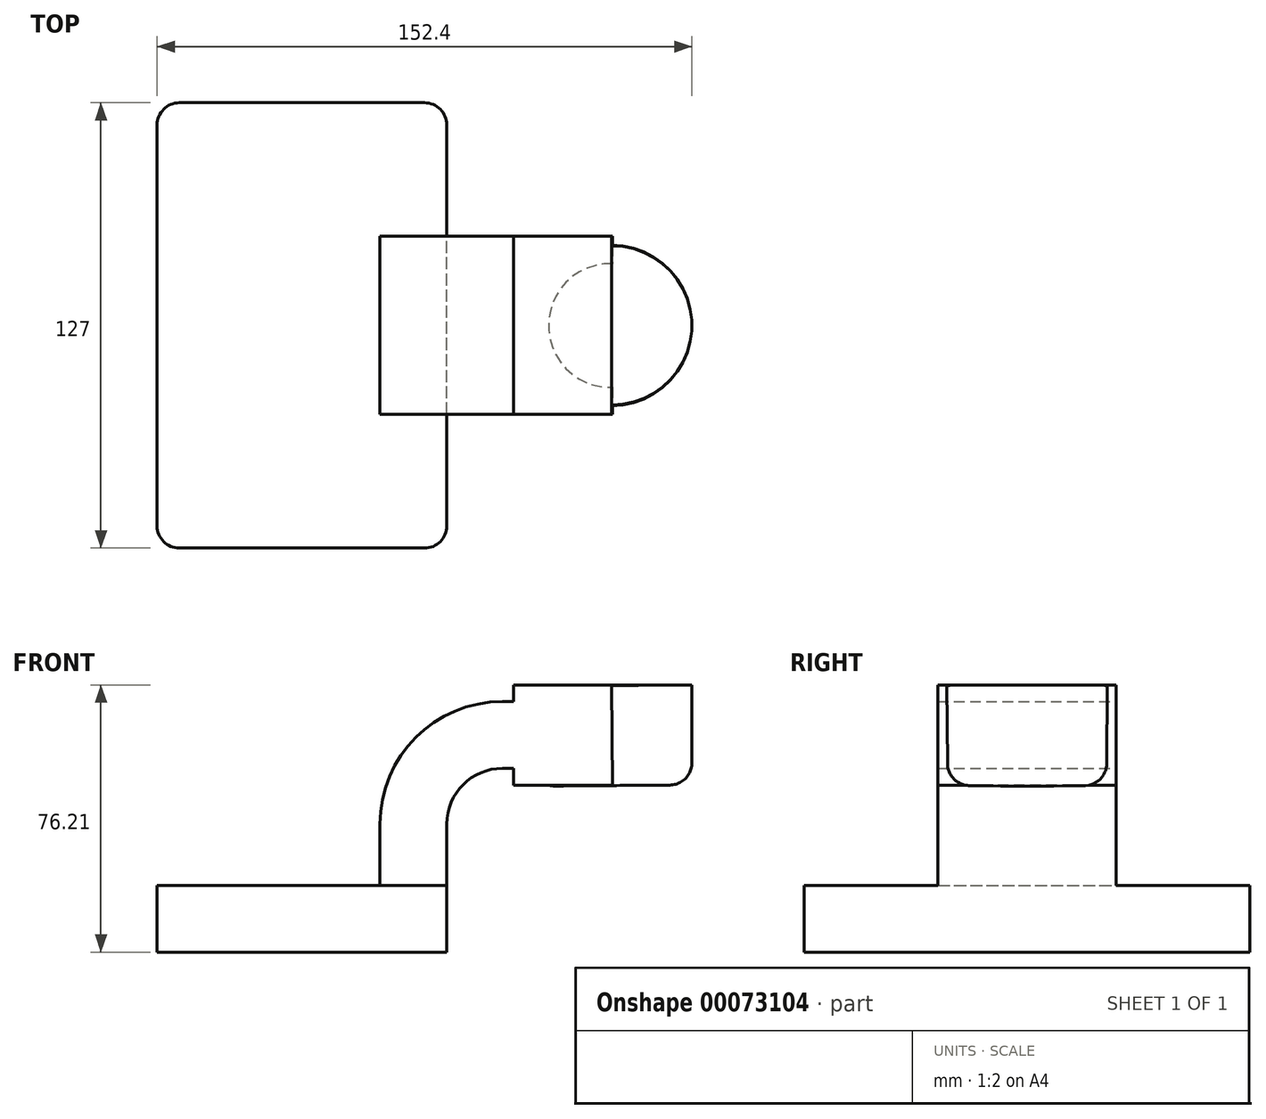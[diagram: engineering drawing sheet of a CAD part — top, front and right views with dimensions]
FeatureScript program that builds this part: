
annotation { "Feature Type Name" : "Feature", "Feature Type Description" : "" }
export const myFeature = defineFeature(function(context is Context, id is Id, definition is map)
    precondition{}
    {
        {
            var Q0;
            Q0=qCreatedBy(makeId("Front.planeOp"),FACE);
            var sketch = newSketch(context, id + "F0", { "sketchPlane" : qUnion([Q0])});
            skLineSegment(sketch, "E0.rect.bottom", {"start": v(-41.28, 9.52) * mm, "end": v(41.27, 9.53) * mm});
            skLineSegment(sketch, "E0.rect.top", {"start": v(-41.28, -9.53) * mm, "end": v(41.28, -9.53) * mm});
            skLineSegment(sketch, "E0.rect.left", {"start": v(-41.28, 9.52) * mm, "end": v(-41.27, -9.53) * mm});
            skLineSegment(sketch, "E0.rect.right", {"start": v(41.28, 9.53) * mm, "end": v(41.28, -9.52) * mm});
            skPoint(sketch, "E0.rect.middle", {"position": v(0, 0) * mm});
            skLineSegment(sketch, "E1.rect.bottom", {"start": v(60.32, 66.68) * mm, "end": v(111.12, 66.68) * mm});
            skLineSegment(sketch, "E1.rect.top", {"start": v(60.32, 38.1) * mm, "end": v(111.12, 38.1) * mm});
            skLineSegment(sketch, "E1.rect.left", {"start": v(60.32, 66.68) * mm, "end": v(60.32, 38.1) * mm});
            skLineSegment(sketch, "E1.rect.right", {"start": v(111.12, 66.68) * mm, "end": v(111.12, 38.1) * mm});
            skPoint(sketch, "E1.rect.middle", {"position": v(85.72, 52.39) * mm});
            skLineSegment(sketch, "E2", {"start": v(41.27, 9.53) * mm, "end": v(41.27, 27) * mm});
            skArc(sketch, "E3", {"start": v(41.27, 27) * mm, "mid": v(45.92, 38.23) * mm, "end": v(57.15, 42.88) * mm});
            skLineSegment(sketch, "E4", {"start": v(57.15, 42.88) * mm, "end": v(88.25, 42.88) * mm});
            skLineSegment(sketch, "E5.0", {"start": v(57.15, 61.93) * mm, "end": v(88.25, 61.93) * mm});
            skArc(sketch, "E5.1", {"start": v(22.22, 27) * mm, "mid": v(32.45, 51.7) * mm, "end": v(57.15, 61.93) * mm});
            skLineSegment(sketch, "E5.2", {"start": v(22.22, 9.53) * mm, "end": v(22.22, 27) * mm});
            skLineSegment(sketch, "E6", {"start": v(88.48, 38.1) * mm, "end": v(88.25, 66.68) * mm});
            skFitSpline(sketch, "E7", {"points": [v(-41.28, 9.52) * mm, v(57.15, 61.93) * mm], "startDerivative": vector(-1.87, 106.27) * mm, "endDerivative": vector(133.08, -17.6) * mm});
            skSolve(sketch);
        }
        {
            var Q0;
            Q0=makeQuery(id+"F0.imprint","IMPRINT",FACE,{"disambiguationData":[TD([[makeQuery(id+"F0.imprint","IMPRINT",EDGE,{"derivedFrom":sQuery(id+"F0.wireOp",EDGE,"E0.rect.top")}),1.0]])]});
            extrude(context, id + "F1", {"entities" : qUnion([Q0]), "endBound" : BoundingType.SYMMETRIC, "depth" : 127 * mm});
        }
        {
            var Q0;
            {var subQ2=sQuery(id+"F0.wireOp",EDGE,"E2");Q0=makeQuery(id+"F0.imprint","IMPRINT",FACE,{"disambiguationData":[TD([[makeQuery(id+"F0.imprint","IMPRINT",EDGE,{"derivedFrom":subQ2}),1.0]])]});}
            var Q1;
            {var subQ7=sQuery(id+"F0.wireOp",EDGE,"E6");Q1=makeQuery(id+"F0.imprint","IMPRINT",FACE,{"disambiguationData":[TD([[makeQuery(id+"F0.imprint","IMPRINT",EDGE,{"derivedFrom":subQ7}),1.0]])]});}
            extrude(context, id + "F2", {"entities" : qUnion([Q0, Q1]), "operationType" : NewBodyOperationType.ADD, "endBound" : BoundingType.SYMMETRIC, "depth" : 50.8 * mm});
        }
        {
            var Q0;
            Q0=makeQuery(id+"F0.imprint","IMPRINT",FACE,{"disambiguationData":[TD([[makeQuery(id+"F0.imprint","IMPRINT",EDGE,{"derivedFrom":sQuery(id+"F0.wireOp",EDGE,"E5.1")}),1.0]])]});
            extrude(context, id + "F3", {"entities" : qUnion([Q0]), "operationType" : NewBodyOperationType.ADD, "endBound" : BoundingType.SYMMETRIC, "depth" : 15.88 * mm});
        }
        {
            var Q0;
            {var subQ0=sQuery(id+"F0.wireOp",EDGE,"E1.rect.right");Q0=makeQuery(id+"F0.imprint","IMPRINT",FACE,{"disambiguationData":[TD([[makeQuery(id+"F0.imprint","IMPRINT",EDGE,{"derivedFrom":subQ0}),-1.0]])]});}
            var Q1;
            Q1=sQuery(id+"F0.wireOp",EDGE,"E6");
            revolve(context, id + "F4", {"operationType" : NewBodyOperationType.ADD, "entities" : qUnion([Q0]), "axis" : qUnion([Q1]), "revolveType" : RevolveType.FULL});
        }
        {
            var Q0;
            Q0=makeQuery(id+"F4.opRevolve","SWEPT_EDGE",EDGE,{"disambiguationData":[OSD([sQuery(id+"F0.wireOp",EDGE,"E1.rect.top"),sQuery(id+"F0.wireOp",EDGE,"E1.rect.right")])]});
            var Q1;
            Q1=makeQuery(id+"F1.opExtrude","CAP_EDGE",EDGE,{"disambiguationData":[OSD([sQuery(id+"F0.wireOp",EDGE,"E0.rect.right")])],"isStart":false});
            var Q2;
            Q2=makeQuery(id+"F1.opExtrude","CAP_EDGE",EDGE,{"disambiguationData":[OSD([sQuery(id+"F0.wireOp",EDGE,"E0.rect.right")])],"isStart":true});
            var Q3;
            Q3=makeQuery(id+"F1.opExtrude","CAP_EDGE",EDGE,{"disambiguationData":[OSD([sQuery(id+"F0.wireOp",EDGE,"E0.rect.left")])],"isStart":true});
            var Q4;
            Q4=makeQuery(id+"F1.opExtrude","CAP_EDGE",EDGE,{"disambiguationData":[OSD([sQuery(id+"F0.wireOp",EDGE,"E0.rect.left")])],"isStart":false});
            fillet(context, id + "F5", {"entities" : qUnion([Q0, Q1, Q2, Q3, Q4]), "radius" : 6.35 * mm, "tangentPropagation" : true, "allowEdgeOverflow" : false});
        }
    });
